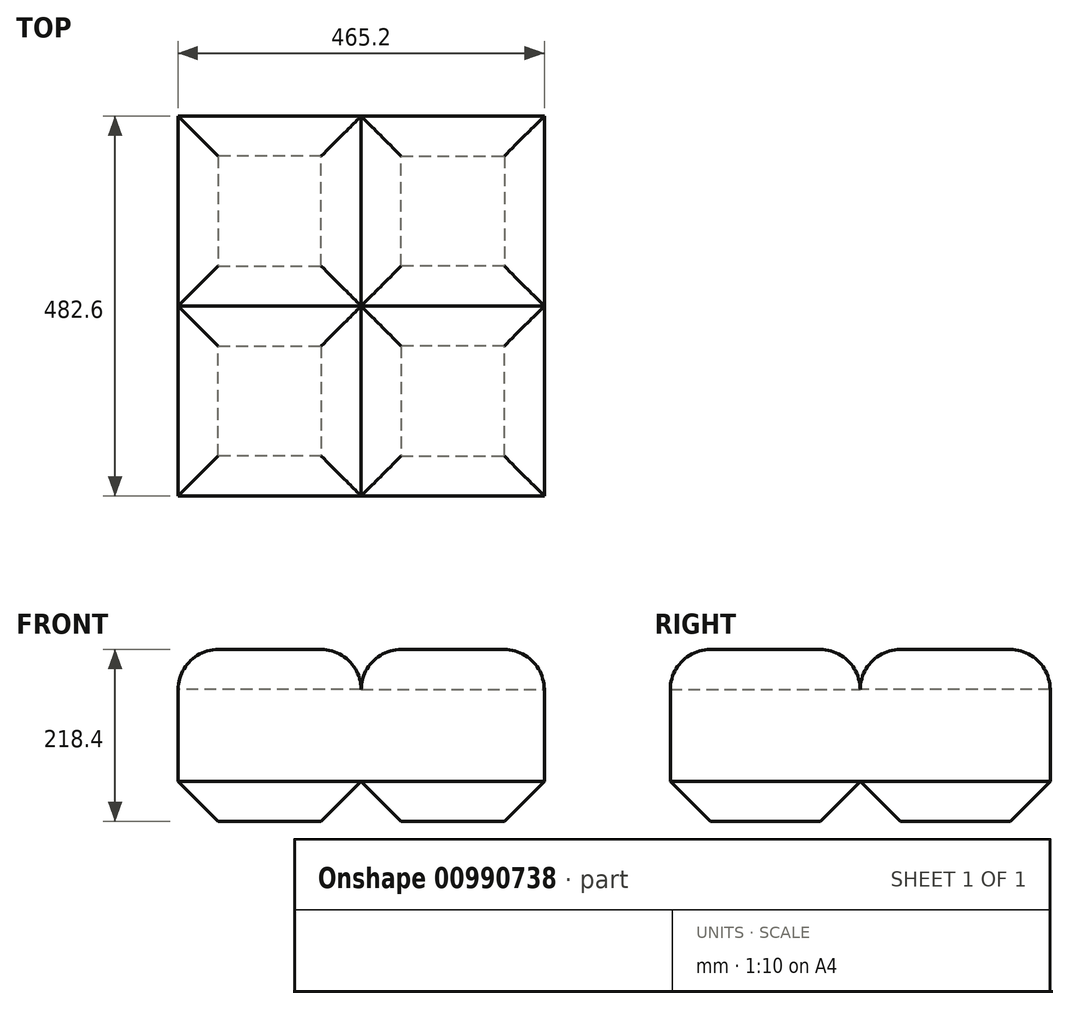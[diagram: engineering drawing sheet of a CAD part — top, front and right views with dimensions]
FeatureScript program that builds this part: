
annotation { "Feature Type Name" : "Feature", "Feature Type Description" : "" }
export const myFeature = defineFeature(function(context is Context, id is Id, definition is map)
    precondition{}
    {
        {
            var Q0;
            Q0=qCreatedBy(makeId("Front.planeOp"),FACE);
            var sketch = newSketch(context, id + "F0", { "sketchPlane" : qUnion([Q0])});
            skLineSegment(sketch, "E0.bottom", {"start": v(116.3, 109.2) * mm, "end": v(-116.3, 109.2) * mm});
            skLineSegment(sketch, "E0.top", {"start": v(116.3, -109.2) * mm, "end": v(-116.3, -109.2) * mm});
            skLineSegment(sketch, "E0.left", {"start": v(116.3, 109.2) * mm, "end": v(116.3, -109.2) * mm});
            skLineSegment(sketch, "E0.right", {"start": v(-116.3, 109.2) * mm, "end": v(-116.3, -109.2) * mm});
            skPoint(sketch, "E0.middle", {"position": v(0, 0) * mm});
            skSolve(sketch);
        }
        {
            var Q0;
            Q0=makeQuery(id+"F0.imprint","IMPRINT",FACE,{"disambiguationData":[TD([[makeQuery(id+"F0.imprint","IMPRINT",EDGE,{"derivedFrom":sQuery(id+"F0.wireOp",EDGE,"E0.bottom")}),1.0]])]});
            extrude(context, id + "F1", {"entities" : qUnion([Q0]), "depth" : 241.3 * mm, "offsetDistance" : 25.4 * mm});
        }
        {
            var Q0;
            Q0=makeQuery(id+"F1.opExtrude","SWEPT_FACE",FACE,{"disambiguationData":[OSD([sQuery(id+"F0.wireOp",EDGE,"E0.bottom")])]});
            fillet(context, id + "F2", {"entities" : qUnion([Q0]), "radius" : 50.8 * mm, "tangentPropagation" : true, "allowEdgeOverflow" : false});
        }
        {
            var Q0;
            Q0=makeQuery(id+"F1.opExtrude","CAP_EDGE",EDGE,{"disambiguationData":[OSD([sQuery(id+"F0.wireOp",EDGE,"E0.top")])],"isStart":false});
            chamfer(context, id + "F3", {"entities" : qUnion([Q0]), "width" : 50.8 * mm, "tangentPropagation" : true});
        }
        {
            var Q0;
            Q0=makeQuery(id+"F1.opExtrude","SWEPT_EDGE",EDGE,{"disambiguationData":[OSD([sQuery(id+"F0.wireOp",EDGE,"E0.top"),sQuery(id+"F0.wireOp",EDGE,"E0.right")])]});
            chamfer(context, id + "F4", {"entities" : qUnion([Q0]), "width" : 50.8 * mm, "tangentPropagation" : true});
        }
        {
            var Q0;
            Q0=makeQuery(id+"F1.opExtrude","CAP_EDGE",EDGE,{"disambiguationData":[OSD([sQuery(id+"F0.wireOp",EDGE,"E0.top")])],"isStart":true});
            var Q1;
            Q1=makeQuery(id+"F1.opExtrude","SWEPT_EDGE",EDGE,{"disambiguationData":[OSD([sQuery(id+"F0.wireOp",EDGE,"E0.top"),sQuery(id+"F0.wireOp",EDGE,"E0.left")])]});
            chamfer(context, id + "F5", {"entities" : qUnion([Q0, Q1]), "width" : 50.8 * mm, "tangentPropagation" : true});
        }
        {
            var Q0;
            Q0=makeQuery(id+"F1.opExtrude","SWEPT_BODY",BODY,{"disambiguationData":[OSD([sQuery(id+"F0.wireOp",EDGE,"E0.bottom"),sQuery(id+"F0.wireOp",EDGE,"E0.top"),sQuery(id+"F0.wireOp",EDGE,"E0.left"),sQuery(id+"F0.wireOp",EDGE,"E0.right")])]});
            var Q1;
            Q1=makeQuery(id+"F1.opExtrude","SWEPT_FACE",FACE,{"disambiguationData":[OSD([sQuery(id+"F0.wireOp",EDGE,"E0.left")])]});
            mirror(context, id + "F6", {"operationType" : NewBodyOperationType.ADD, "entities" : qUnion([Q0]), "mirrorPlane" : qUnion([Q1])});
        }
        {
            var Q0;
            Q0=makeQuery(id+"F1.opExtrude","SWEPT_BODY",BODY,{"disambiguationData":[OSD([sQuery(id+"F0.wireOp",EDGE,"E0.bottom"),sQuery(id+"F0.wireOp",EDGE,"E0.top"),sQuery(id+"F0.wireOp",EDGE,"E0.left"),sQuery(id+"F0.wireOp",EDGE,"E0.right")])]});
            var Q1;
            {var subQ0=makeQuery(id+"F1.opExtrude","CAP_FACE",FACE,{"disambiguationData":[OSD([sQuery(id+"F0.wireOp",EDGE,"E0.bottom"),sQuery(id+"F0.wireOp",EDGE,"E0.top"),sQuery(id+"F0.wireOp",EDGE,"E0.left"),sQuery(id+"F0.wireOp",EDGE,"E0.right")])],"isStart":true});Q1=makeQuery(id+"F6.boolean.opBoolean","MERGE",FACE,{"derivedFrom":[subQ0,makeQuery(id+"F6.opPattern","COPY",FACE,{"derivedFrom":subQ0,"instanceName":"1"})]});}
            mirror(context, id + "F7", {"operationType" : NewBodyOperationType.ADD, "entities" : qUnion([Q0]), "mirrorPlane" : qUnion([Q1])});
        }
    });
